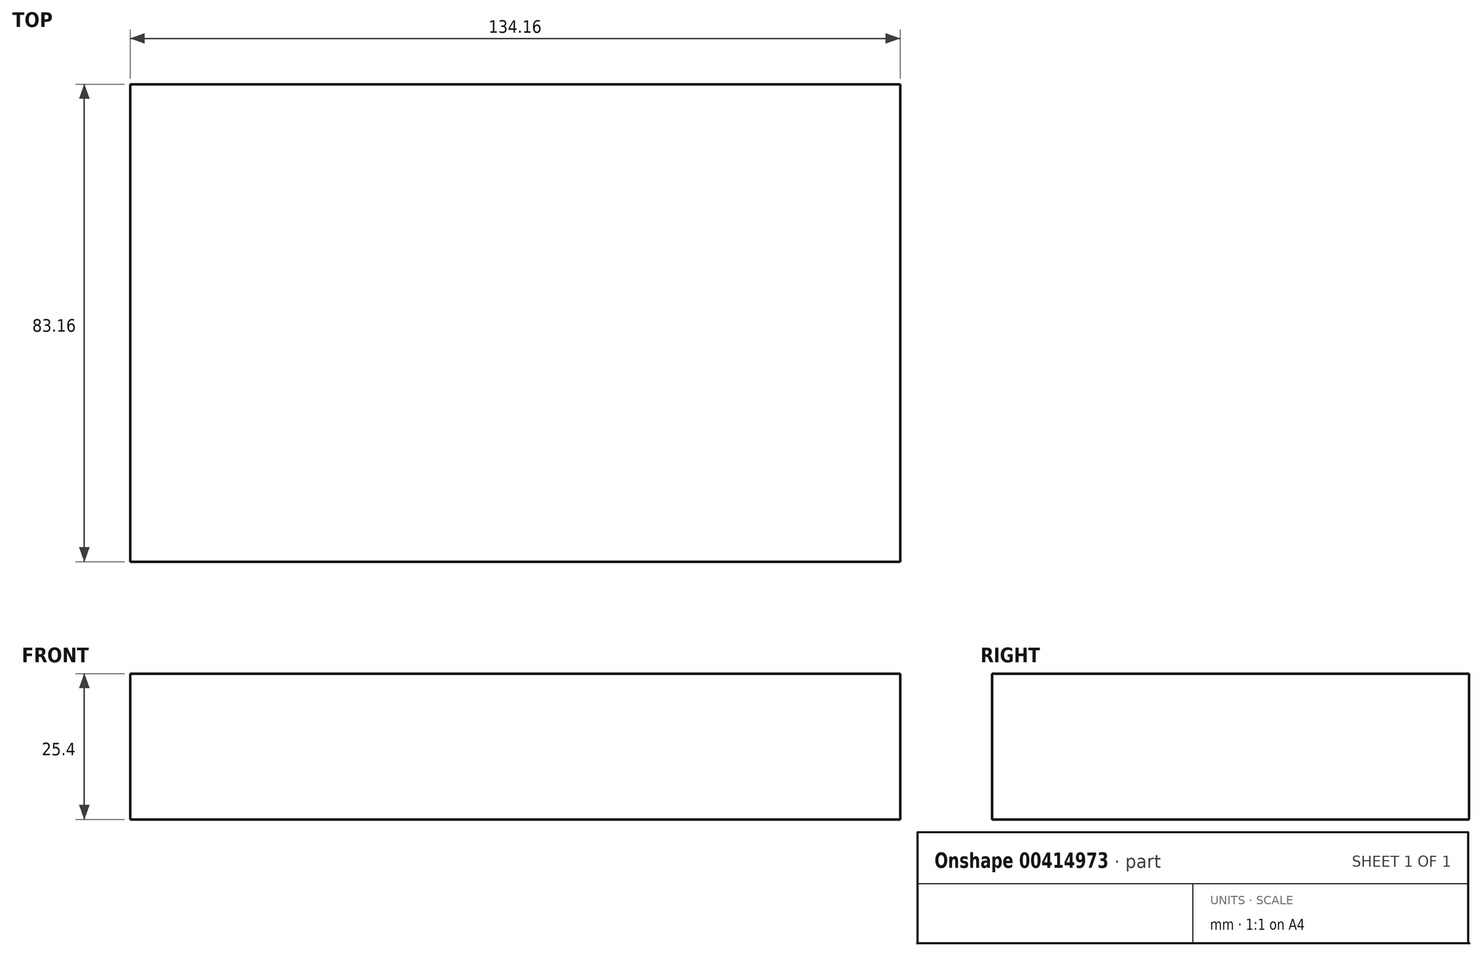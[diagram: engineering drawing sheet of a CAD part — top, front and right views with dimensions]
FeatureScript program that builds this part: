
annotation { "Feature Type Name" : "Feature", "Feature Type Description" : "" }
export const myFeature = defineFeature(function(context is Context, id is Id, definition is map)
    precondition{}
    {
        {
            var Q0;
            Q0=qCreatedBy(makeId("Top.planeOp"),FACE);
            var sketch = newSketch(context, id + "F0", { "sketchPlane" : qUnion([Q0])});
            skLineSegment(sketch, "E0.bottom", {"start": v(-67.08, 41.58) * mm, "end": v(67.08, 41.58) * mm});
            skLineSegment(sketch, "E0.top", {"start": v(-67.08, -41.58) * mm, "end": v(67.08, -41.58) * mm});
            skLineSegment(sketch, "E0.left", {"start": v(-67.08, 41.58) * mm, "end": v(-67.08, -41.58) * mm});
            skLineSegment(sketch, "E0.right", {"start": v(67.08, 41.58) * mm, "end": v(67.08, -41.58) * mm});
            skPoint(sketch, "E0.middle", {"position": v(0, 0) * mm});
            skSolve(sketch);
        }
        {
            var Q0;
            Q0 = qSketchRegion(id + "F0", true);
            extrude(context, id + "F1", {"entities" : qUnion([Q0]), "depth" : 25.4 * mm});
        }
    });
